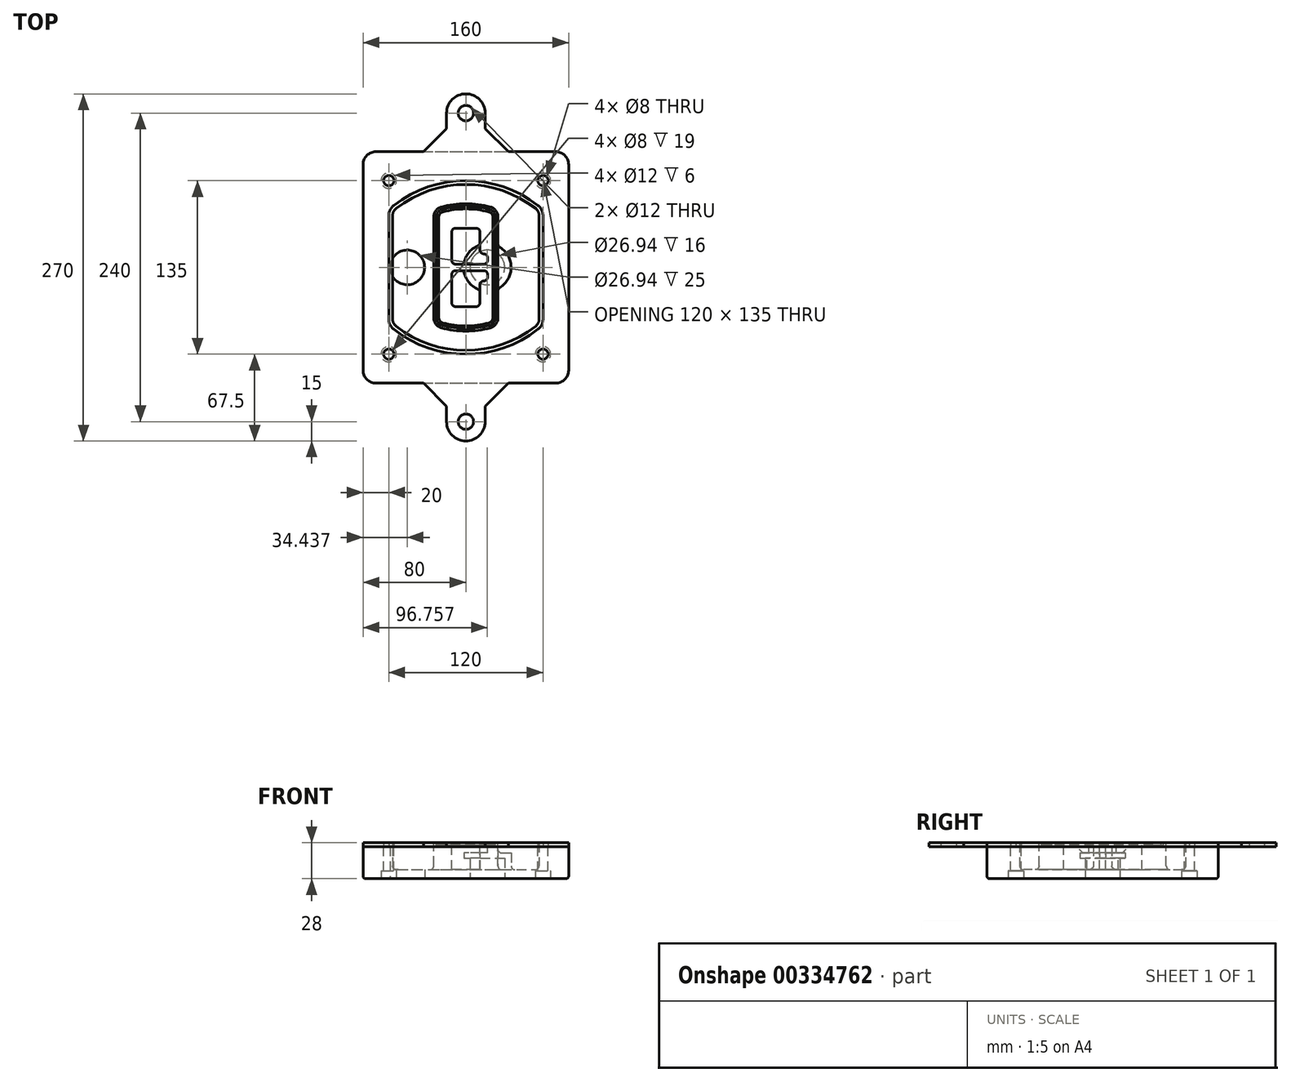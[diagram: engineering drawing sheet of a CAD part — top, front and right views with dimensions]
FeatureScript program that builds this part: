
annotation { "Feature Type Name" : "Feature", "Feature Type Description" : "" }
export const myFeature = defineFeature(function(context is Context, id is Id, definition is map)
    precondition{}
    {
        {
            var Q0;
            Q0=qCreatedBy(makeId("Top.planeOp"),FACE);
            var sketch = newSketch(context, id + "F0", { "sketchPlane" : qUnion([Q0])});
            skPoint(sketch, "E0.rect.middle", {"position": v(0, 0) * mm});
            skLineSegment(sketch, "E1.bottom", {"start": v(-70, -90) * mm, "end": v(70, -90) * mm});
            skLineSegment(sketch, "E1.top", {"start": v(-70, 90) * mm, "end": v(70, 90) * mm});
            skLineSegment(sketch, "E1.left", {"start": v(-80, -80) * mm, "end": v(-80, 80) * mm});
            skLineSegment(sketch, "E1.right", {"start": v(80, -80) * mm, "end": v(80, 80) * mm});
            skLineSegment(sketch, "E2", {"start": v(-80, 90) * mm, "end": v(80, -90) * mm, "construction": true});
            skLineSegment(sketch, "E3", {"start": v(80, 90) * mm, "end": v(-80, -90) * mm, "construction": true});
            skCircle(sketch, "E4", {"center": v(-60, 67.5) * mm, "radius": 4 * mm});
            skCircle(sketch, "E5", {"center": v(60, 67.5) * mm, "radius": 4 * mm});
            skCircle(sketch, "E6", {"center": v(60, -67.5) * mm, "radius": 4 * mm});
            skCircle(sketch, "E7", {"center": v(-60, -67.5) * mm, "radius": 4 * mm});
            skLineSegment(sketch, "E8", {"start": v(-60, 67.5) * mm, "end": v(60, 67.5) * mm, "construction": true});
            skLineSegment(sketch, "E9", {"start": v(60, 67.5) * mm, "end": v(60, -67.5) * mm, "construction": true});
            skLineSegment(sketch, "E10", {"start": v(60, -67.5) * mm, "end": v(-60, -67.5) * mm, "construction": true});
            skLineSegment(sketch, "E11", {"start": v(-60, -67.5) * mm, "end": v(-60, 67.5) * mm, "construction": true});
            skLineSegment(sketch, "E12", {"start": v(-60, 40.3) * mm, "end": v(-60, -40.3) * mm});
            skLineSegment(sketch, "E13", {"start": v(60, 40.3) * mm, "end": v(60, -40.3) * mm});
            skArc(sketch, "E14", {"start": v(56.15, 48.18) * mm, "mid": v(0, 67.5) * mm, "end": v(-56.15, 48.18) * mm});
            skArc(sketch, "E15", {"start": v(-56.15, -48.18) * mm, "mid": v(0, -67.5) * mm, "end": v(56.15, -48.18) * mm});
            skLineSegment(sketch, "E16", {"start": v(-60, 0) * mm, "end": v(60, 0) * mm, "construction": true});
            skPoint(sketch, "E17.visualSharp", {"position": v(-60, -45) * mm});
            skArc(sketch, "E17.filletArc", {"start": v(-60, -40.3) * mm, "mid": v(-58.99, -44.68) * mm, "end": v(-56.15, -48.18) * mm});
            skPoint(sketch, "E18.visualSharp", {"position": v(-60, 45) * mm});
            skArc(sketch, "E18.filletArc", {"start": v(-56.15, 48.18) * mm, "mid": v(-58.99, 44.68) * mm, "end": v(-60, 40.3) * mm});
            skPoint(sketch, "E19.visualSharp", {"position": v(60, 45) * mm});
            skArc(sketch, "E19.filletArc", {"start": v(60, 40.3) * mm, "mid": v(58.99, 44.68) * mm, "end": v(56.15, 48.18) * mm});
            skPoint(sketch, "E20.visualSharp", {"position": v(60, -45) * mm});
            skArc(sketch, "E20.filletArc", {"start": v(56.15, -48.18) * mm, "mid": v(58.99, -44.68) * mm, "end": v(60, -40.3) * mm});
            skPoint(sketch, "E21.visualSharp", {"position": v(-80, 90) * mm});
            skArc(sketch, "E21.filletArc", {"start": v(-70, 90) * mm, "mid": v(-77.07, 87.07) * mm, "end": v(-80, 80) * mm});
            skPoint(sketch, "E22.visualSharp", {"position": v(80, 90) * mm});
            skArc(sketch, "E22.filletArc", {"start": v(80, 80) * mm, "mid": v(77.07, 87.07) * mm, "end": v(70, 90) * mm});
            skPoint(sketch, "E23.visualSharp", {"position": v(80, -90) * mm});
            skArc(sketch, "E23.filletArc", {"start": v(70, -90) * mm, "mid": v(77.07, -87.07) * mm, "end": v(80, -80) * mm});
            skPoint(sketch, "E24.visualSharp", {"position": v(-80, -90) * mm});
            skArc(sketch, "E24.filletArc", {"start": v(-80, -80) * mm, "mid": v(-77.07, -87.07) * mm, "end": v(-70, -90) * mm});
            skArc(sketch, "E25.0", {"start": v(57, 40.3) * mm, "mid": v(56.3, 43.36) * mm, "end": v(54.3, 45.81) * mm});
            skLineSegment(sketch, "E25.1", {"start": v(57, 40.3) * mm, "end": v(57, -40.3) * mm});
            skArc(sketch, "E25.2", {"start": v(54.3, -45.81) * mm, "mid": v(56.3, -43.36) * mm, "end": v(57, -40.3) * mm});
            skArc(sketch, "E25.3", {"start": v(-54.3, -45.81) * mm, "mid": v(0, -64.5) * mm, "end": v(54.3, -45.81) * mm});
            skArc(sketch, "E25.4", {"start": v(-57, -40.3) * mm, "mid": v(-56.3, -43.36) * mm, "end": v(-54.3, -45.81) * mm});
            skArc(sketch, "E25.5", {"start": v(54.3, 45.81) * mm, "mid": v(0, 64.5) * mm, "end": v(-54.3, 45.81) * mm});
            skLineSegment(sketch, "E25.6", {"start": v(-57, 40.3) * mm, "end": v(-57, -40.3) * mm});
            skArc(sketch, "E25.7", {"start": v(-54.3, 45.81) * mm, "mid": v(-56.3, 43.36) * mm, "end": v(-57, 40.3) * mm});
            skArc(sketch, "E26.0", {"start": v(-58.62, 51.33) * mm, "mid": v(-62.58, 46.43) * mm, "end": v(-64, 40.3) * mm});
            skArc(sketch, "E26.1", {"start": v(58.62, 51.33) * mm, "mid": v(0, 71.5) * mm, "end": v(-58.62, 51.33) * mm});
            skArc(sketch, "E26.2", {"start": v(64, 40.3) * mm, "mid": v(62.58, 46.43) * mm, "end": v(58.62, 51.33) * mm});
            skLineSegment(sketch, "E26.3", {"start": v(64, 40.3) * mm, "end": v(64, -40.3) * mm});
            skArc(sketch, "E26.4", {"start": v(58.62, -51.33) * mm, "mid": v(62.58, -46.43) * mm, "end": v(64, -40.3) * mm});
            skLineSegment(sketch, "E26.5", {"start": v(-64, 40.3) * mm, "end": v(-64, -40.3) * mm});
            skArc(sketch, "E26.6", {"start": v(-58.62, -51.33) * mm, "mid": v(0, -71.5) * mm, "end": v(58.62, -51.33) * mm});
            skArc(sketch, "E26.7", {"start": v(-64, -40.3) * mm, "mid": v(-62.58, -46.43) * mm, "end": v(-58.62, -51.33) * mm});
            skSolve(sketch);
        }
        {
            var Q0;
            Q0=makeQuery(id+"F0.imprint","IMPRINT",FACE,{"disambiguationData":[TD([[makeQuery(id+"F0.imprint","IMPRINT",EDGE,{"derivedFrom":sQuery(id+"F0.wireOp",EDGE,"E1.bottom")}),1.0]])]});
            var Q1;
            Q1=makeQuery(id+"F0.imprint","IMPRINT",FACE,{"disambiguationData":[TD([[makeQuery(id+"F0.imprint","IMPRINT",EDGE,{"derivedFrom":sQuery(id+"F0.wireOp",EDGE,"E12")}),1.0]])]});
            var Q2;
            Q2=makeQuery(id+"F0.imprint","IMPRINT",FACE,{"disambiguationData":[TD([[makeQuery(id+"F0.imprint","IMPRINT",EDGE,{"derivedFrom":sQuery(id+"F0.wireOp",EDGE,"E25.0")}),1.0]])]});
            var Q3;
            Q3=makeQuery(id+"F0.imprint","IMPRINT",FACE,{"disambiguationData":[TD([[makeQuery(id+"F0.imprint","IMPRINT",EDGE,{"derivedFrom":sQuery(id+"F0.wireOp",EDGE,"E12")}),-1.0]])]});
            extrude(context, id + "F1", {"entities" : qUnion([Q0, Q1, Q2, Q3]), "oppositeDirection" : true, "depth" : 25 * mm});
        }
        {
            var Q0;
            Q0=makeQuery(id+"F0.imprint","IMPRINT",FACE,{"disambiguationData":[TD([[makeQuery(id+"F0.imprint","IMPRINT",EDGE,{"derivedFrom":sQuery(id+"F0.wireOp",EDGE,"E12")}),1.0]])]});
            extrude(context, id + "F2", {"entities" : qUnion([Q0]), "operationType" : NewBodyOperationType.ADD, "depth" : 3 * mm});
        }
        {
            var Q0;
            Q0=makeQuery(id+"F0.imprint","IMPRINT",FACE,{"disambiguationData":[TD([[makeQuery(id+"F0.imprint","IMPRINT",EDGE,{"derivedFrom":sQuery(id+"F0.wireOp",EDGE,"E25.0")}),1.0]])]});
            extrude(context, id + "F3", {"entities" : qUnion([Q0]), "operationType" : NewBodyOperationType.REMOVE, "oppositeDirection" : true, "depth" : 18 * mm});
        }
        {
            var Q0;
            Q0=makeQuery(id+"F2.opExtrude","CAP_FACE",FACE,{"disambiguationData":[OSD([sQuery(id+"F0.wireOp",EDGE,"E12"),sQuery(id+"F0.wireOp",EDGE,"E13"),sQuery(id+"F0.wireOp",EDGE,"E14"),sQuery(id+"F0.wireOp",EDGE,"E15"),sQuery(id+"F0.wireOp",EDGE,"E17.filletArc"),sQuery(id+"F0.wireOp",EDGE,"E18.filletArc"),sQuery(id+"F0.wireOp",EDGE,"E19.filletArc"),sQuery(id+"F0.wireOp",EDGE,"E20.filletArc"),sQuery(id+"F0.wireOp",EDGE,"E25.0"),sQuery(id+"F0.wireOp",EDGE,"E25.1"),sQuery(id+"F0.wireOp",EDGE,"E25.2"),sQuery(id+"F0.wireOp",EDGE,"E25.3"),sQuery(id+"F0.wireOp",EDGE,"E25.4"),sQuery(id+"F0.wireOp",EDGE,"E25.5"),sQuery(id+"F0.wireOp",EDGE,"E25.6"),sQuery(id+"F0.wireOp",EDGE,"E25.7")])],"isStart":false});
            var sketch = newSketch(context, id + "F4", { "sketchPlane" : qUnion([Q0])});
            skArc(sketch, "E27.0", {"start": v(-19.08, -46.97) * mm, "mid": v(0, -49.5) * mm, "end": v(19.08, -46.97) * mm});
            skArc(sketch, "E28.0", {"start": v(19.08, 46.97) * mm, "mid": v(0, 49.5) * mm, "end": v(-19.08, 46.97) * mm});
            skLineSegment(sketch, "E29", {"start": v(-25, 39.25) * mm, "end": v(-25, -39.25) * mm});
            skLineSegment(sketch, "E30", {"start": v(25, 39.25) * mm, "end": v(25, -39.25) * mm});
            skLineSegment(sketch, "E31", {"start": v(-25, 45.1) * mm, "end": v(25, 45.1) * mm, "construction": true});
            skLineSegment(sketch, "E32", {"start": v(-25, -45.1) * mm, "end": v(25, -45.1) * mm, "construction": true});
            skPoint(sketch, "E33.visualSharp", {"position": v(-25, 45.1) * mm});
            skArc(sketch, "E33.filletArc", {"start": v(-19.08, 46.97) * mm, "mid": v(-23.35, 44.11) * mm, "end": v(-25, 39.25) * mm});
            skPoint(sketch, "E34.visualSharp", {"position": v(25, 45.1) * mm});
            skArc(sketch, "E34.filletArc", {"start": v(25, 39.25) * mm, "mid": v(23.35, 44.11) * mm, "end": v(19.08, 46.97) * mm});
            skPoint(sketch, "E35.visualSharp", {"position": v(25, -45.1) * mm});
            skArc(sketch, "E35.filletArc", {"start": v(19.08, -46.97) * mm, "mid": v(23.35, -44.11) * mm, "end": v(25, -39.25) * mm});
            skPoint(sketch, "E36.visualSharp", {"position": v(-25, -45.1) * mm});
            skArc(sketch, "E36.filletArc", {"start": v(-25, -39.25) * mm, "mid": v(-23.35, -44.11) * mm, "end": v(-19.08, -46.97) * mm});
            skArc(sketch, "E37.0", {"start": v(54.3, 45.81) * mm, "mid": v(0, 64.5) * mm, "end": v(-54.3, 45.81) * mm});
            skArc(sketch, "E37.1", {"start": v(-54.3, 45.81) * mm, "mid": v(-56.3, 43.36) * mm, "end": v(-57, 40.3) * mm});
            skLineSegment(sketch, "E37.2", {"start": v(-57, 40.3) * mm, "end": v(-57, -40.3) * mm});
            skArc(sketch, "E37.3", {"start": v(-57, -40.3) * mm, "mid": v(-56.3, -43.36) * mm, "end": v(-54.3, -45.81) * mm});
            skArc(sketch, "E37.4", {"start": v(-54.3, -45.81) * mm, "mid": v(0, -64.5) * mm, "end": v(54.3, -45.81) * mm});
            skArc(sketch, "E37.5", {"start": v(54.3, -45.81) * mm, "mid": v(56.3, -43.36) * mm, "end": v(57, -40.3) * mm});
            skLineSegment(sketch, "E37.6", {"start": v(57, 40.3) * mm, "end": v(57, -40.3) * mm});
            skArc(sketch, "E37.7", {"start": v(57, 40.3) * mm, "mid": v(56.3, 43.36) * mm, "end": v(54.3, 45.81) * mm});
            skLineSegment(sketch, "E38.0", {"start": v(23, 39.25) * mm, "end": v(23, -39.25) * mm});
            skArc(sketch, "E38.1", {"start": v(18.56, -45.04) * mm, "mid": v(21.76, -42.9) * mm, "end": v(23, -39.25) * mm});
            skArc(sketch, "E38.2", {"start": v(-18.56, -45.04) * mm, "mid": v(0, -47.5) * mm, "end": v(18.56, -45.04) * mm});
            skArc(sketch, "E38.3", {"start": v(-23, -39.25) * mm, "mid": v(-21.76, -42.9) * mm, "end": v(-18.56, -45.04) * mm});
            skLineSegment(sketch, "E38.4", {"start": v(-23, 39.25) * mm, "end": v(-23, -39.25) * mm});
            skArc(sketch, "E38.5", {"start": v(23, 39.25) * mm, "mid": v(21.76, 42.9) * mm, "end": v(18.56, 45.04) * mm});
            skArc(sketch, "E38.6", {"start": v(-18.56, 45.04) * mm, "mid": v(-21.76, 42.9) * mm, "end": v(-23, 39.25) * mm});
            skArc(sketch, "E38.7", {"start": v(18.56, 45.04) * mm, "mid": v(0, 47.5) * mm, "end": v(-18.56, 45.04) * mm});
            skArc(sketch, "E39.0", {"start": v(21, 39.25) * mm, "mid": v(20.18, 41.68) * mm, "end": v(18.04, 43.1) * mm});
            skLineSegment(sketch, "E39.1", {"start": v(21, 39.25) * mm, "end": v(21, -39.25) * mm});
            skArc(sketch, "E39.2", {"start": v(18.04, -43.1) * mm, "mid": v(20.18, -41.68) * mm, "end": v(21, -39.25) * mm});
            skArc(sketch, "E39.3", {"start": v(-18.04, -43.1) * mm, "mid": v(0, -45.5) * mm, "end": v(18.04, -43.1) * mm});
            skArc(sketch, "E39.4", {"start": v(-21, -39.25) * mm, "mid": v(-20.18, -41.68) * mm, "end": v(-18.04, -43.1) * mm});
            skArc(sketch, "E39.5", {"start": v(18.04, 43.1) * mm, "mid": v(0, 45.5) * mm, "end": v(-18.04, 43.1) * mm});
            skLineSegment(sketch, "E39.6", {"start": v(-21, 39.25) * mm, "end": v(-21, -39.25) * mm});
            skArc(sketch, "E39.7", {"start": v(-18.04, 43.1) * mm, "mid": v(-20.18, 41.68) * mm, "end": v(-21, 39.25) * mm});
            skLineSegment(sketch, "E40", {"start": v(-25, 0) * mm, "end": v(25, 0) * mm, "construction": true});
            skLineSegment(sketch, "E41", {"start": v(-11, 5.5) * mm, "end": v(-11, 27.5) * mm});
            skLineSegment(sketch, "E42", {"start": v(-8, 30.5) * mm, "end": v(8, 30.5) * mm});
            skLineSegment(sketch, "E43", {"start": v(11, 27.5) * mm, "end": v(11, 13.5) * mm});
            skLineSegment(sketch, "E44", {"start": v(14, 10.5) * mm, "end": v(14, 10.5) * mm});
            skLineSegment(sketch, "E45", {"start": v(17, 7.5) * mm, "end": v(17, 5.5) * mm});
            skLineSegment(sketch, "E46", {"start": v(14, 2.5) * mm, "end": v(-8, 2.5) * mm});
            skPoint(sketch, "E47.visualSharp", {"position": v(-11, 30.5) * mm});
            skArc(sketch, "E47.filletArc", {"start": v(-8, 30.5) * mm, "mid": v(-10.12, 29.62) * mm, "end": v(-11, 27.5) * mm});
            skPoint(sketch, "E48.visualSharp", {"position": v(11, 30.5) * mm});
            skArc(sketch, "E48.filletArc", {"start": v(11, 27.5) * mm, "mid": v(10.12, 29.62) * mm, "end": v(8, 30.5) * mm});
            skPoint(sketch, "E49.visualSharp", {"position": v(11, 10.5) * mm});
            skArc(sketch, "E49.filletArc", {"start": v(11, 13.5) * mm, "mid": v(11.88, 11.38) * mm, "end": v(14, 10.5) * mm});
            skPoint(sketch, "E50.visualSharp", {"position": v(17, 10.5) * mm});
            skArc(sketch, "E50.filletArc", {"start": v(17, 7.5) * mm, "mid": v(16.12, 9.62) * mm, "end": v(14, 10.5) * mm});
            skPoint(sketch, "E51.visualSharp", {"position": v(17, 2.5) * mm});
            skArc(sketch, "E51.filletArc", {"start": v(14, 2.5) * mm, "mid": v(16.12, 3.38) * mm, "end": v(17, 5.5) * mm});
            skPoint(sketch, "E52.visualSharp", {"position": v(-11, 2.5) * mm});
            skArc(sketch, "E52.filletArc", {"start": v(-11, 5.5) * mm, "mid": v(-10.12, 3.38) * mm, "end": v(-8, 2.5) * mm});
            skLineSegment(sketch, "E53.0.MirrorCS", {"start": v(14, -2.5) * mm, "end": v(-8, -2.5) * mm});
            skArc(sketch, "E54.0.MirrorCS", {"start": v(-11, -5.5) * mm, "mid": v(-10.12, -3.38) * mm, "end": v(-8, -2.5) * mm});
            skLineSegment(sketch, "E55.0.MirrorCS", {"start": v(-11, -5.5) * mm, "end": v(-11, -27.5) * mm});
            skArc(sketch, "E56.0.MirrorCS", {"start": v(-8, -30.5) * mm, "mid": v(-10.12, -29.62) * mm, "end": v(-11, -27.5) * mm});
            skLineSegment(sketch, "E57.0.MirrorCS", {"start": v(-8, -30.5) * mm, "end": v(8, -30.5) * mm});
            skArc(sketch, "E58.0.MirrorCS", {"start": v(11, -27.5) * mm, "mid": v(10.12, -29.62) * mm, "end": v(8, -30.5) * mm});
            skLineSegment(sketch, "E59.0.MirrorCS", {"start": v(11, -27.5) * mm, "end": v(11, -13.5) * mm});
            skArc(sketch, "E60.0.MirrorCS", {"start": v(11, -13.5) * mm, "mid": v(11.88, -11.38) * mm, "end": v(14, -10.5) * mm});
            skArc(sketch, "E61.0.MirrorCS", {"start": v(17, -7.5) * mm, "mid": v(16.12, -9.62) * mm, "end": v(14, -10.5) * mm});
            skLineSegment(sketch, "E62.0.MirrorCS", {"start": v(17, -7.5) * mm, "end": v(17, -5.5) * mm});
            skArc(sketch, "E63.0.MirrorCS", {"start": v(14, -2.5) * mm, "mid": v(16.12, -3.38) * mm, "end": v(17, -5.5) * mm});
            skSolve(sketch);
        }
        {
            var Q0;
            Q0=makeQuery(id+"F4.imprint","IMPRINT",FACE,{"disambiguationData":[TD([[makeQuery(id+"F4.imprint","IMPRINT",EDGE,{"derivedFrom":sQuery(id+"F4.wireOp",EDGE,"E27.0")}),1.0]])]});
            var Q1;
            Q1=makeQuery(id+"F4.imprint","IMPRINT",FACE,{"disambiguationData":[TD([[makeQuery(id+"F4.imprint","IMPRINT",EDGE,{"derivedFrom":sQuery(id+"F4.wireOp",EDGE,"E38.0")}),-1.0]])]});
            var Q2;
            Q2=makeQuery(id+"F4.imprint","IMPRINT",FACE,{"disambiguationData":[TD([[makeQuery(id+"F4.imprint","IMPRINT",EDGE,{"derivedFrom":sQuery(id+"F4.wireOp",EDGE,"E39.0")}),1.0]])]});
            extrude(context, id + "F5", {"entities" : qUnion([Q0, Q1, Q2]), "operationType" : NewBodyOperationType.ADD, "endBound" : BoundingType.UP_TO_NEXT, "oppositeDirection" : true, "depth" : 25 * mm});
        }
        {
            var Q0;
            Q0=makeQuery(id+"F4.imprint","IMPRINT",FACE,{"disambiguationData":[TD([[makeQuery(id+"F4.imprint","IMPRINT",EDGE,{"derivedFrom":sQuery(id+"F4.wireOp",EDGE,"E38.0")}),-1.0]])]});
            extrude(context, id + "F6", {"entities" : qUnion([Q0]), "operationType" : NewBodyOperationType.REMOVE, "oppositeDirection" : true, "depth" : 2 * mm});
        }
        {
            var Q0;
            Q0=makeQuery(id+"F1.opExtrude","CAP_FACE",FACE,{"disambiguationData":[OSD([sQuery(id+"F0.wireOp",EDGE,"E1.bottom"),sQuery(id+"F0.wireOp",EDGE,"E1.top"),sQuery(id+"F0.wireOp",EDGE,"E1.left"),sQuery(id+"F0.wireOp",EDGE,"E1.right"),sQuery(id+"F0.wireOp",EDGE,"E4"),sQuery(id+"F0.wireOp",EDGE,"E5"),sQuery(id+"F0.wireOp",EDGE,"E6"),sQuery(id+"F0.wireOp",EDGE,"E7"),sQuery(id+"F0.wireOp",EDGE,"E21.filletArc"),sQuery(id+"F0.wireOp",EDGE,"E22.filletArc"),sQuery(id+"F0.wireOp",EDGE,"E23.filletArc"),sQuery(id+"F0.wireOp",EDGE,"E24.filletArc")])],"isStart":false});
            var sketch = newSketch(context, id + "F7", { "sketchPlane" : qUnion([Q0])});
            skCircle(sketch, "E64", {"center": v(16.76, 0) * mm, "radius": 13.47 * mm});
            skCircle(sketch, "E65", {"center": v(-45.56, 0) * mm, "radius": 13.47 * mm});
            skLineSegment(sketch, "E66", {"start": v(80, 0) * mm, "end": v(-80, 0) * mm});
            skCircle(sketch, "E67", {"center": v(16.76, 0) * mm, "radius": 18.47 * mm});
            skCircle(sketch, "E68", {"center": v(60, -67.5) * mm, "radius": 6 * mm});
            skCircle(sketch, "E69", {"center": v(-60, -67.5) * mm, "radius": 6 * mm});
            skCircle(sketch, "E70", {"center": v(-60, 67.5) * mm, "radius": 6 * mm});
            skCircle(sketch, "E71", {"center": v(60, 67.5) * mm, "radius": 6 * mm});
            skSolve(sketch);
        }
        {
            var Q0;
            {var subQ1=sQuery(id+"F7.wireOp",EDGE,"E66");var subQ4=sQuery(id+"F7.wireOp",EDGE,"E64");var subQ6=makeQuery(id+"F7.imprint","INTERSECT",VERTEX,{"disambiguationData":[OD(0.0)],"derivedFrom":[subQ4,subQ1]});Q0=makeQuery(id+"F7.imprint","IMPRINT",FACE,{"disambiguationData":[TD([[makeQuery(id+"F7.imprint","IMPRINT",EDGE,{"disambiguationData":[TD([[subQ6,-1.0]])],"derivedFrom":subQ4}),-1.0]])]});}
            var Q1;
            {var subQ0=sQuery(id+"F7.wireOp",EDGE,"E66");var subQ1=sQuery(id+"F7.wireOp",EDGE,"E64");var subQ3=makeQuery(id+"F7.imprint","INTERSECT",VERTEX,{"disambiguationData":[OD(0.0)],"derivedFrom":[subQ1,subQ0]});Q1=makeQuery(id+"F7.imprint","IMPRINT",FACE,{"disambiguationData":[TD([[makeQuery(id+"F7.imprint","IMPRINT",EDGE,{"disambiguationData":[TD([[subQ3,-1.0]])],"derivedFrom":subQ1}),1.0]])]});}
            var Q2;
            {var subQ0=sQuery(id+"F7.wireOp",EDGE,"E66");var subQ1=sQuery(id+"F7.wireOp",EDGE,"E64");var subQ3=makeQuery(id+"F7.imprint","INTERSECT",VERTEX,{"disambiguationData":[OD(0.0)],"derivedFrom":[subQ1,subQ0]});Q2=makeQuery(id+"F7.imprint","IMPRINT",FACE,{"disambiguationData":[TD([[makeQuery(id+"F7.imprint","IMPRINT",EDGE,{"disambiguationData":[TD([[subQ3,1.0]])],"derivedFrom":subQ1}),1.0]])]});}
            var Q3;
            {var subQ1=sQuery(id+"F7.wireOp",EDGE,"E66");var subQ4=sQuery(id+"F7.wireOp",EDGE,"E64");var subQ6=makeQuery(id+"F7.imprint","INTERSECT",VERTEX,{"disambiguationData":[OD(0.0)],"derivedFrom":[subQ4,subQ1]});Q3=makeQuery(id+"F7.imprint","IMPRINT",FACE,{"disambiguationData":[TD([[makeQuery(id+"F7.imprint","IMPRINT",EDGE,{"disambiguationData":[TD([[subQ6,1.0]])],"derivedFrom":subQ4}),-1.0]])]});}
            extrude(context, id + "F8", {"entities" : qUnion([Q0, Q1, Q2, Q3]), "operationType" : NewBodyOperationType.ADD, "oppositeDirection" : true, "depth" : 20 * mm});
        }
        {
            var Q0;
            {var subQ0=sQuery(id+"F7.wireOp",EDGE,"E66");var subQ1=sQuery(id+"F7.wireOp",EDGE,"E64");var subQ3=makeQuery(id+"F7.imprint","INTERSECT",VERTEX,{"disambiguationData":[OD(0.0)],"derivedFrom":[subQ1,subQ0]});Q0=makeQuery(id+"F7.imprint","IMPRINT",FACE,{"disambiguationData":[TD([[makeQuery(id+"F7.imprint","IMPRINT",EDGE,{"disambiguationData":[TD([[subQ3,-1.0]])],"derivedFrom":subQ1}),1.0]])]});}
            var Q1;
            {var subQ0=sQuery(id+"F7.wireOp",EDGE,"E66");var subQ1=sQuery(id+"F7.wireOp",EDGE,"E64");var subQ3=makeQuery(id+"F7.imprint","INTERSECT",VERTEX,{"disambiguationData":[OD(0.0)],"derivedFrom":[subQ1,subQ0]});Q1=makeQuery(id+"F7.imprint","IMPRINT",FACE,{"disambiguationData":[TD([[makeQuery(id+"F7.imprint","IMPRINT",EDGE,{"disambiguationData":[TD([[subQ3,1.0]])],"derivedFrom":subQ1}),1.0]])]});}
            extrude(context, id + "F9", {"entities" : qUnion([Q0, Q1]), "operationType" : NewBodyOperationType.REMOVE, "oppositeDirection" : true, "depth" : 16 * mm});
        }
        {
            var Q0;
            {var subQ0=sQuery(id+"F7.wireOp",EDGE,"E66");var subQ1=sQuery(id+"F7.wireOp",EDGE,"E65");var subQ3=makeQuery(id+"F7.imprint","INTERSECT",VERTEX,{"disambiguationData":[OD(0.0)],"derivedFrom":[subQ1,subQ0]});Q0=makeQuery(id+"F7.imprint","IMPRINT",FACE,{"disambiguationData":[TD([[makeQuery(id+"F7.imprint","IMPRINT",EDGE,{"disambiguationData":[TD([[subQ3,-1.0]])],"derivedFrom":subQ1}),1.0]])]});}
            var Q1;
            {var subQ0=sQuery(id+"F7.wireOp",EDGE,"E66");var subQ1=sQuery(id+"F7.wireOp",EDGE,"E65");var subQ3=makeQuery(id+"F7.imprint","INTERSECT",VERTEX,{"disambiguationData":[OD(0.0)],"derivedFrom":[subQ1,subQ0]});Q1=makeQuery(id+"F7.imprint","IMPRINT",FACE,{"disambiguationData":[TD([[makeQuery(id+"F7.imprint","IMPRINT",EDGE,{"disambiguationData":[TD([[subQ3,1.0]])],"derivedFrom":subQ1}),1.0]])]});}
            extrude(context, id + "F10", {"entities" : qUnion([Q0, Q1]), "operationType" : NewBodyOperationType.REMOVE, "oppositeDirection" : true, "depth" : 25 * mm});
        }
        {
            var Q0;
            Q0=makeQuery(id+"F7.imprint","IMPRINT",FACE,{"disambiguationData":[TD([[makeQuery(id+"F7.imprint","IMPRINT",EDGE,{"derivedFrom":sQuery(id+"F7.wireOp",EDGE,"E68")}),1.0]])]});
            var Q1;
            Q1=makeQuery(id+"F7.imprint","IMPRINT",FACE,{"disambiguationData":[TD([[makeQuery(id+"F7.imprint","IMPRINT",EDGE,{"derivedFrom":makeQuery(id+"F1.opExtrude","CAP_EDGE",EDGE,{"disambiguationData":[OSD([sQuery(id+"F0.wireOp",EDGE,"E5")])],"isStart":false})}),-1.0]])]});
            var Q2;
            Q2=makeQuery(id+"F7.imprint","IMPRINT",FACE,{"disambiguationData":[TD([[makeQuery(id+"F7.imprint","IMPRINT",EDGE,{"derivedFrom":sQuery(id+"F7.wireOp",EDGE,"E69")}),1.0]])]});
            var Q3;
            Q3=makeQuery(id+"F7.imprint","IMPRINT",FACE,{"disambiguationData":[TD([[makeQuery(id+"F7.imprint","IMPRINT",EDGE,{"derivedFrom":makeQuery(id+"F1.opExtrude","CAP_EDGE",EDGE,{"disambiguationData":[OSD([sQuery(id+"F0.wireOp",EDGE,"E4")])],"isStart":false})}),-1.0]])]});
            var Q4;
            Q4=makeQuery(id+"F7.imprint","IMPRINT",FACE,{"disambiguationData":[TD([[makeQuery(id+"F7.imprint","IMPRINT",EDGE,{"derivedFrom":sQuery(id+"F7.wireOp",EDGE,"E70")}),1.0]])]});
            var Q5;
            Q5=makeQuery(id+"F7.imprint","IMPRINT",FACE,{"disambiguationData":[TD([[makeQuery(id+"F7.imprint","IMPRINT",EDGE,{"derivedFrom":makeQuery(id+"F1.opExtrude","CAP_EDGE",EDGE,{"disambiguationData":[OSD([sQuery(id+"F0.wireOp",EDGE,"E7")])],"isStart":false})}),-1.0]])]});
            var Q6;
            Q6=makeQuery(id+"F7.imprint","IMPRINT",FACE,{"disambiguationData":[TD([[makeQuery(id+"F7.imprint","IMPRINT",EDGE,{"derivedFrom":sQuery(id+"F7.wireOp",EDGE,"E71")}),1.0]])]});
            var Q7;
            Q7=makeQuery(id+"F7.imprint","IMPRINT",FACE,{"disambiguationData":[TD([[makeQuery(id+"F7.imprint","IMPRINT",EDGE,{"derivedFrom":makeQuery(id+"F1.opExtrude","CAP_EDGE",EDGE,{"disambiguationData":[OSD([sQuery(id+"F0.wireOp",EDGE,"E6")])],"isStart":false})}),-1.0]])]});
            extrude(context, id + "F11", {"entities" : qUnion([Q0, Q1, Q2, Q3, Q4, Q5, Q6, Q7]), "operationType" : NewBodyOperationType.REMOVE, "oppositeDirection" : true, "depth" : 6 * mm});
        }
        {
            var Q0;
            Q0=makeQuery(id+"F9.boolean.opBoolean","COPY",FACE,{"derivedFrom":makeQuery(id+"F9.opExtrude","CAP_FACE",FACE,{"disambiguationData":[OSD([sQuery(id+"F7.wireOp",EDGE,"E64")])],"isStart":false})});
            var sketch = newSketch(context, id + "F12", { "sketchPlane" : qUnion([Q0])});
            skArc(sketch, "E72.0", {"start": v(11, 17.55) * mm, "mid": v(2.57, 11.82) * mm, "end": v(-1.54, 2.5) * mm});
            skArc(sketch, "E72.1", {"start": v(-1.54, -2.5) * mm, "mid": v(2.57, -11.82) * mm, "end": v(11, -17.55) * mm});
            skLineSegment(sketch, "E73", {"start": v(-1.54, -2.5) * mm, "end": v(14, -2.5) * mm});
            skLineSegment(sketch, "E74.0", {"start": v(14, 2.5) * mm, "end": v(-1.54, 2.5) * mm});
            skArc(sketch, "E74.1", {"start": v(14, 2.5) * mm, "mid": v(16.12, 3.38) * mm, "end": v(17, 5.5) * mm});
            skLineSegment(sketch, "E74.2", {"start": v(17, 7.5) * mm, "end": v(17, 5.5) * mm});
            skArc(sketch, "E74.3", {"start": v(17, 7.5) * mm, "mid": v(16.12, 9.62) * mm, "end": v(14, 10.5) * mm});
            skArc(sketch, "E74.4", {"start": v(11, 13.5) * mm, "mid": v(11.88, 11.38) * mm, "end": v(14, 10.5) * mm});
            skLineSegment(sketch, "E74.5", {"start": v(11, 17.55) * mm, "end": v(11, 13.5) * mm});
            skLineSegment(sketch, "E74.7", {"start": v(14, -2.5) * mm, "end": v(-1.54, -2.5) * mm});
            skArc(sketch, "E74.8", {"start": v(14, -2.5) * mm, "mid": v(16.12, -3.38) * mm, "end": v(17, -5.5) * mm});
            skLineSegment(sketch, "E74.9", {"start": v(17, -7.5) * mm, "end": v(17, -5.5) * mm});
            skArc(sketch, "E74.10", {"start": v(17, -7.5) * mm, "mid": v(16.12, -9.62) * mm, "end": v(14, -10.5) * mm});
            skArc(sketch, "E74.11", {"start": v(11, -13.5) * mm, "mid": v(11.88, -11.38) * mm, "end": v(14, -10.5) * mm});
            skLineSegment(sketch, "E74.12", {"start": v(11, -17.55) * mm, "end": v(11, -13.5) * mm});
            skPoint(sketch, "E75.orphan", {"position": v(11, -27.5) * mm});
            skPoint(sketch, "E76.orphan", {"position": v(-8, -2.5) * mm});
            skPoint(sketch, "E77.orphan", {"position": v(-8, 2.5) * mm});
            skPoint(sketch, "E78.orphan", {"position": v(11, 27.5) * mm});
            skSolve(sketch);
        }
        {
            var Q0;
            {var subQ7=sQuery(id+"F12.wireOp",EDGE,"E72.0");var subQ14=sQuery(id+"F12.wireOp",EDGE,"E72.1");var subQ16=sQuery(id+"F12.wireOp",EDGE,"E74.1");var subQ18=sQuery(id+"F12.wireOp",EDGE,"E74.8");Q0=qUnion([makeQuery(id+"F12.imprint","IMPRINT",FACE,{"disambiguationData":[TD([[makeQuery(id+"F12.imprint","IMPRINT",EDGE,{"derivedFrom":subQ7}),1.0]])]}),makeQuery(id+"F12.imprint","IMPRINT",FACE,{"disambiguationData":[TD([[makeQuery(id+"F12.imprint","IMPRINT",EDGE,{"derivedFrom":subQ14}),1.0]])]}),makeQuery(id+"F12.imprint","IMPRINT",FACE,{"disambiguationData":[TD([[makeQuery(id+"F12.imprint","IMPRINT",EDGE,{"derivedFrom":subQ16}),1.0]])]}),makeQuery(id+"F12.imprint","IMPRINT",FACE,{"disambiguationData":[TD([[makeQuery(id+"F12.imprint","IMPRINT",EDGE,{"derivedFrom":subQ18}),-1.0]])]})]);}
            var Q1;
            Q1=makeQuery(id+"F5.boolean.opBoolean","SPLIT",FACE,{"disambiguationData":[TD([makeQuery(id+"F5.opExtrude","SWEPT_FACE",FACE,{"disambiguationData":[OSD([sQuery(id+"F4.wireOp",EDGE,"E41")])]})])],"derivedFrom":makeQuery(id+"F3.boolean.opBoolean","COPY",FACE,{"derivedFrom":makeQuery(id+"F3.opExtrude","CAP_FACE",FACE,{"disambiguationData":[OSD([sQuery(id+"F0.wireOp",EDGE,"E25.0"),sQuery(id+"F0.wireOp",EDGE,"E25.1"),sQuery(id+"F0.wireOp",EDGE,"E25.2"),sQuery(id+"F0.wireOp",EDGE,"E25.3"),sQuery(id+"F0.wireOp",EDGE,"E25.4"),sQuery(id+"F0.wireOp",EDGE,"E25.5"),sQuery(id+"F0.wireOp",EDGE,"E25.6"),sQuery(id+"F0.wireOp",EDGE,"E25.7")])],"isStart":false})})});
            extrude(context, id + "F13", {"entities" : qUnion([Q0]), "operationType" : NewBodyOperationType.REMOVE, "endBound" : BoundingType.UP_TO_SURFACE, "endBoundEntityFace" : qUnion([Q1]), "depth" : 25 * mm});
        }
        {
            var Q0;
            Q0=makeQuery(id+"F3.boolean.opBoolean","COPY",EDGE,{"derivedFrom":makeQuery(id+"F3.opExtrude","CAP_EDGE",EDGE,{"disambiguationData":[OSD([sQuery(id+"F0.wireOp",EDGE,"E25.6")])],"isStart":false})});
            var Q1;
            Q1=makeQuery(id+"F8.boolean.opBoolean","INTERSECT",EDGE,{"derivedFrom":[makeQuery(id+"F5.opExtrude","SWEPT_FACE",FACE,{"disambiguationData":[OSD([sQuery(id+"F4.wireOp",EDGE,"E30")])]}),makeQuery(id+"F8.opExtrude","CAP_FACE",FACE,{"disambiguationData":[OSD([sQuery(id+"F7.wireOp",EDGE,"E67")])],"isStart":false})]});
            var Q2;
            Q2=makeQuery(id+"F8.boolean.opBoolean","INTERSECT",EDGE,{"disambiguationData":[OD(1.0)],"derivedFrom":[makeQuery(id+"F5.opExtrude","SWEPT_FACE",FACE,{"disambiguationData":[OSD([sQuery(id+"F4.wireOp",EDGE,"E30")])]}),makeQuery(id+"F8.opExtrude","SWEPT_FACE",FACE,{"disambiguationData":[OSD([sQuery(id+"F7.wireOp",EDGE,"E67")])]})]});
            var Q3;
            {var subQ0=sQuery(id+"F4.wireOp",EDGE,"E30");Q3=makeQuery(id+"F8.boolean.opBoolean","SPLIT",EDGE,{"disambiguationData":[TD([makeQuery(id+"F5.opExtrude","SWEPT_FACE",FACE,{"disambiguationData":[OSD([sQuery(id+"F4.wireOp",EDGE,"E35.filletArc")])]})])],"derivedFrom":makeQuery(id+"F5.opExtrude","CAP_EDGE",EDGE,{"disambiguationData":[OSD([subQ0])],"isStart":false})});}
            var Q4;
            {var subQ0=sQuery(id+"F0.wireOp",EDGE,"E25.7");var subQ1=sQuery(id+"F0.wireOp",EDGE,"E25.1");var subQ2=sQuery(id+"F0.wireOp",EDGE,"E25.6");var subQ3=sQuery(id+"F0.wireOp",EDGE,"E25.5");var subQ4=sQuery(id+"F0.wireOp",EDGE,"E25.4");var subQ5=sQuery(id+"F0.wireOp",EDGE,"E25.0");var subQ6=sQuery(id+"F0.wireOp",EDGE,"E25.2");var subQ7=sQuery(id+"F0.wireOp",EDGE,"E25.3");Q4=makeQuery(id+"F8.boolean.opBoolean","INTERSECT",EDGE,{"derivedFrom":[makeQuery(id+"F5.boolean.opBoolean","SPLIT",FACE,{"disambiguationData":[TD([makeQuery(id+"F2.opExtrude","SWEPT_FACE",FACE,{"disambiguationData":[OSD([subQ5])]})])],"derivedFrom":makeQuery(id+"F3.boolean.opBoolean","COPY",FACE,{"derivedFrom":makeQuery(id+"F3.opExtrude","CAP_FACE",FACE,{"disambiguationData":[OSD([subQ5,subQ1,subQ6,subQ7,subQ4,subQ3,subQ2,subQ0])],"isStart":false})})}),makeQuery(id+"F8.opExtrude","SWEPT_FACE",FACE,{"disambiguationData":[OSD([sQuery(id+"F7.wireOp",EDGE,"E67")])]})]});}
            var Q5;
            Q5=makeQuery(id+"F8.boolean.opBoolean","INTERSECT",EDGE,{"disambiguationData":[OD(0.0)],"derivedFrom":[makeQuery(id+"F5.opExtrude","SWEPT_FACE",FACE,{"disambiguationData":[OSD([sQuery(id+"F4.wireOp",EDGE,"E30")])]}),makeQuery(id+"F8.opExtrude","SWEPT_FACE",FACE,{"disambiguationData":[OSD([sQuery(id+"F7.wireOp",EDGE,"E67")])]})]});
            fillet(context, id + "F14", {"entities" : qUnion([Q0, Q1, Q2, Q3, Q4, Q5]), "radius" : 3 * mm, "tangentPropagation" : true, "allowEdgeOverflow" : false});
        }
        {
            var Q0;
            Q0=makeQuery(id+"F1.opExtrude","CAP_EDGE",EDGE,{"disambiguationData":[OSD([sQuery(id+"F0.wireOp",EDGE,"E1.bottom")])],"isStart":false});
            fillet(context, id + "F15", {"entities" : qUnion([Q0]), "radius" : 2 * mm, "tangentPropagation" : true, "allowEdgeOverflow" : false});
        }
        {
            var Q0;
            {var subQ0=sQuery(id+"F0.wireOp",EDGE,"E21.filletArc");var subQ1=sQuery(id+"F0.wireOp",EDGE,"E7");var subQ2=sQuery(id+"F0.wireOp",EDGE,"E6");var subQ3=sQuery(id+"F0.wireOp",EDGE,"E5");var subQ4=sQuery(id+"F0.wireOp",EDGE,"E4");var subQ5=sQuery(id+"F0.wireOp",EDGE,"E22.filletArc");var subQ6=sQuery(id+"F0.wireOp",EDGE,"E1.bottom");var subQ7=sQuery(id+"F0.wireOp",EDGE,"E1.right");var subQ8=sQuery(id+"F0.wireOp",EDGE,"E1.top");var subQ9=sQuery(id+"F0.wireOp",EDGE,"E1.left");var subQ10=sQuery(id+"F0.wireOp",EDGE,"E23.filletArc");var subQ11=sQuery(id+"F0.wireOp",EDGE,"E24.filletArc");Q0=makeQuery(id+"F2.boolean.opBoolean","SPLIT",FACE,{"disambiguationData":[TD([makeQuery(id+"F1.opExtrude","SWEPT_FACE",FACE,{"disambiguationData":[OSD([subQ6])]})])],"derivedFrom":makeQuery(id+"F1.opExtrude","CAP_FACE",FACE,{"disambiguationData":[OSD([subQ6,subQ8,subQ9,subQ7,subQ4,subQ3,subQ2,subQ1,subQ0,subQ5,subQ10,subQ11])],"isStart":true})});}
            var sketch = newSketch(context, id + "F16", { "sketchPlane" : qUnion([Q0])});
            skLineSegment(sketch, "E79", {"start": v(0, 90) * mm, "end": v(0, 120) * mm, "construction": true});
            skCircle(sketch, "E80", {"center": v(0, 120) * mm, "radius": 6 * mm});
            skLineSegment(sketch, "E81", {"start": v(-33, 90) * mm, "end": v(-15, 108) * mm});
            skLineSegment(sketch, "E82", {"start": v(33, 90) * mm, "end": v(15, 108) * mm});
            skLineSegment(sketch, "E83", {"start": v(-15, 108) * mm, "end": v(-15, 120) * mm});
            skLineSegment(sketch, "E84", {"start": v(15, 108) * mm, "end": v(15, 120) * mm});
            skArc(sketch, "E85", {"start": v(15, 120) * mm, "mid": v(0, 135) * mm, "end": v(-15, 120) * mm});
            skLineSegment(sketch, "E86", {"start": v(-80, 0) * mm, "end": v(80, 0) * mm, "construction": true});
            skLineSegment(sketch, "E87.MirrorCS", {"start": v(15, -108) * mm, "end": v(15, -120) * mm});
            skArc(sketch, "E88.MirrorCS", {"start": v(15, -120) * mm, "mid": v(0, -135) * mm, "end": v(-15, -120) * mm});
            skLineSegment(sketch, "E89.MirrorCS", {"start": v(0, -90) * mm, "end": v(0, -120) * mm, "construction": true});
            skCircle(sketch, "E90.MirrorC", {"center": v(0, -120) * mm, "radius": 6 * mm});
            skLineSegment(sketch, "E91.MirrorCS", {"start": v(-15, -108) * mm, "end": v(-15, -120) * mm});
            skLineSegment(sketch, "E92.MirrorCS", {"start": v(-33, -90) * mm, "end": v(-15, -108) * mm});
            skLineSegment(sketch, "E93.MirrorCS", {"start": v(33, -90) * mm, "end": v(15, -108) * mm});
            skSolve(sketch);
        }
        {
            var Q0;
            Q0=makeQuery(id+"F16.imprint","IMPRINT",FACE,{"disambiguationData":[TD([[makeQuery(id+"F16.imprint","IMPRINT",EDGE,{"derivedFrom":makeQuery(id+"F1.opExtrude","CAP_EDGE",EDGE,{"disambiguationData":[OSD([sQuery(id+"F0.wireOp",EDGE,"E1.left")])],"isStart":true})}),-1.0]])]});
            var Q1;
            Q1=makeQuery(id+"F16.imprint","IMPRINT",FACE,{"disambiguationData":[TD([[makeQuery(id+"F16.imprint","IMPRINT",EDGE,{"derivedFrom":sQuery(id+"F16.wireOp",EDGE,"E87.MirrorCS")}),-1.0]])]});
            var Q2;
            Q2=makeQuery(id+"F16.imprint","IMPRINT",FACE,{"disambiguationData":[TD([[makeQuery(id+"F16.imprint","IMPRINT",EDGE,{"derivedFrom":sQuery(id+"F16.wireOp",EDGE,"E80")}),-1.0]])]});
            var Q3;
            Q3=makeQuery(id+"F2.opExtrude","CAP_FACE",FACE,{"disambiguationData":[OSD([sQuery(id+"F0.wireOp",EDGE,"E12"),sQuery(id+"F0.wireOp",EDGE,"E13"),sQuery(id+"F0.wireOp",EDGE,"E14"),sQuery(id+"F0.wireOp",EDGE,"E15"),sQuery(id+"F0.wireOp",EDGE,"E17.filletArc"),sQuery(id+"F0.wireOp",EDGE,"E18.filletArc"),sQuery(id+"F0.wireOp",EDGE,"E19.filletArc"),sQuery(id+"F0.wireOp",EDGE,"E20.filletArc"),sQuery(id+"F0.wireOp",EDGE,"E25.0"),sQuery(id+"F0.wireOp",EDGE,"E25.1"),sQuery(id+"F0.wireOp",EDGE,"E25.2"),sQuery(id+"F0.wireOp",EDGE,"E25.3"),sQuery(id+"F0.wireOp",EDGE,"E25.4"),sQuery(id+"F0.wireOp",EDGE,"E25.5"),sQuery(id+"F0.wireOp",EDGE,"E25.6"),sQuery(id+"F0.wireOp",EDGE,"E25.7")])],"isStart":false});
            extrude(context, id + "F17", {"entities" : qUnion([Q0, Q1, Q2]), "endBound" : BoundingType.UP_TO_SURFACE, "endBoundEntityFace" : qUnion([Q3]), "depth" : 25 * mm});
        }
    });
